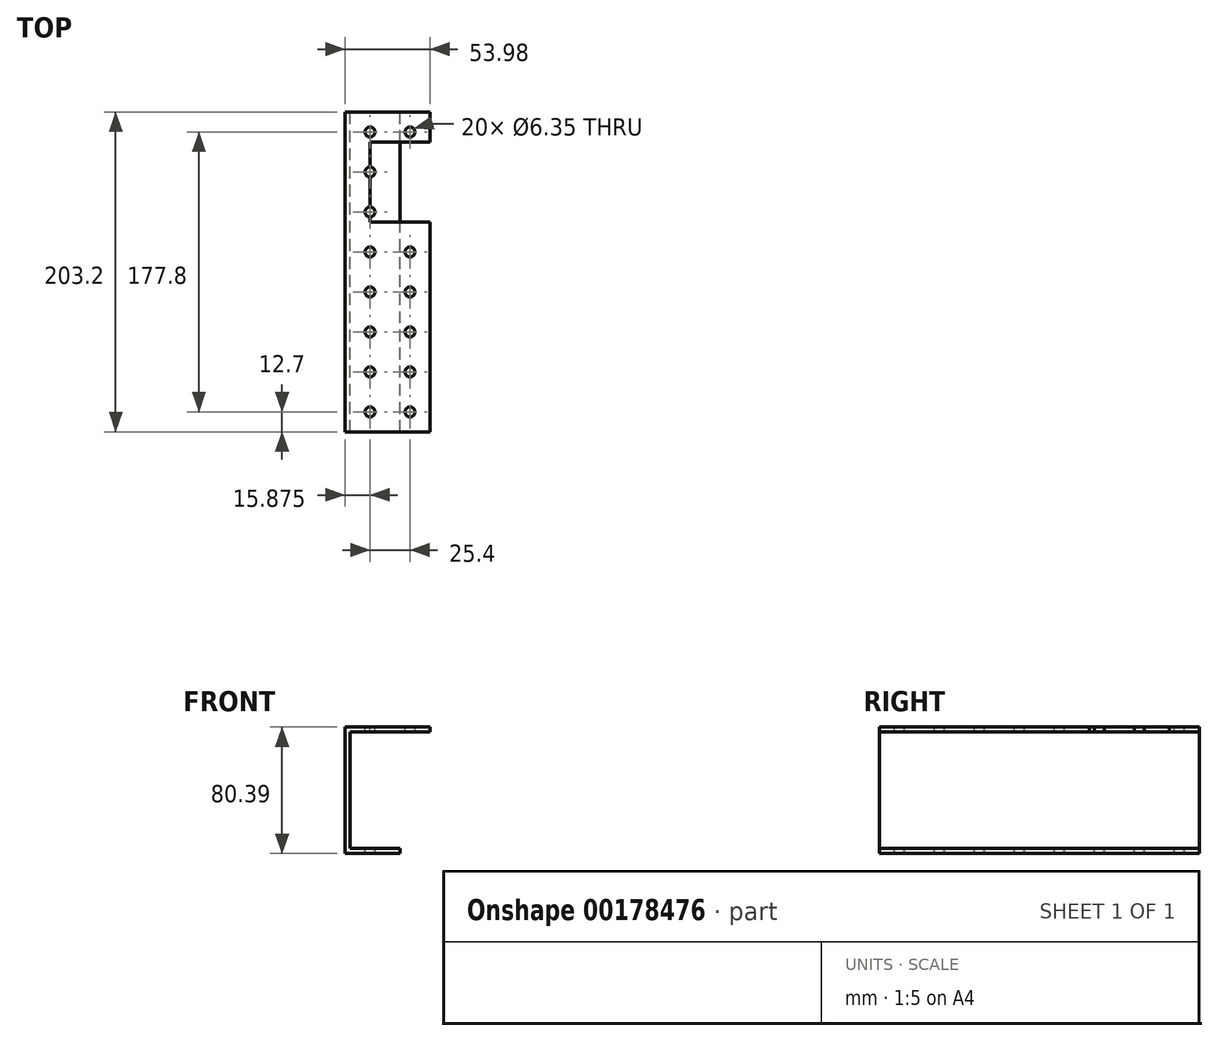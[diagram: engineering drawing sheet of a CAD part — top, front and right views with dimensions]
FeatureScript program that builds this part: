
annotation { "Feature Type Name" : "Feature", "Feature Type Description" : "" }
export const myFeature = defineFeature(function(context is Context, id is Id, definition is map)
    precondition{}
    {
        {
            var Q0;
            Q0=qCreatedBy(makeId("Front.planeOp"),FACE);
            var sketch = newSketch(context, id + "F0", { "sketchPlane" : qUnion([Q0])});
            skLineSegment(sketch, "E0", {"start": v(0, 44.52) * mm, "end": v(0, -35.87) * mm});
            skLineSegment(sketch, "E1", {"start": v(0, 44.52) * mm, "end": v(53.98, 44.52) * mm});
            skLineSegment(sketch, "E2", {"start": v(0, -35.87) * mm, "end": v(34.93, -35.87) * mm});
            skLineSegment(sketch, "E3", {"start": v(34.93, -35.87) * mm, "end": v(34.93, -32.7) * mm});
            skLineSegment(sketch, "E4", {"start": v(34.93, -32.7) * mm, "end": v(3.18, -32.7) * mm});
            skLineSegment(sketch, "E5", {"start": v(3.18, -32.7) * mm, "end": v(3.18, 41.34) * mm});
            skLineSegment(sketch, "E6", {"start": v(3.18, 41.34) * mm, "end": v(53.98, 41.34) * mm});
            skLineSegment(sketch, "E7", {"start": v(53.98, 41.34) * mm, "end": v(53.98, 44.52) * mm});
            skSolve(sketch);
        }
        {
            var Q0;
            Q0=makeQuery(id+"F0.imprint","IMPRINT",FACE,{"disambiguationData":[TD([[makeQuery(id+"F0.imprint","IMPRINT",EDGE,{"derivedFrom":sQuery(id+"F0.wireOp",EDGE,"E0")}),1.0]])]});
            extrude(context, id + "F1", {"entities" : qUnion([Q0]), "depth" : 203.2 * mm});
        }
        {
            var Q0;
            Q0=makeQuery(id+"F1.opExtrude","SWEPT_FACE",FACE,{"disambiguationData":[OSD([sQuery(id+"F0.wireOp",EDGE,"E1")])]});
            var sketch = newSketch(context, id + "F2", { "sketchPlane" : qUnion([Q0])});
            skLineSegment(sketch, "E8.bottom", {"start": v(53.98, -19.05) * mm, "end": v(15.87, -19.05) * mm});
            skLineSegment(sketch, "E8.top", {"start": v(53.98, -69.85) * mm, "end": v(15.88, -69.85) * mm});
            skLineSegment(sketch, "E8.left", {"start": v(53.98, -19.05) * mm, "end": v(53.98, -69.85) * mm});
            skLineSegment(sketch, "E8.right", {"start": v(15.87, -19.05) * mm, "end": v(15.88, -69.85) * mm});
            skLineSegment(sketch, "E9", {"start": v(15.24, -37.47) * mm, "end": v(15.24, -18.42) * mm});
            skLineSegment(sketch, "E10", {"start": v(15.24, -18.42) * mm, "end": v(-22.86, -18.42) * mm});
            skLineSegment(sketch, "E11", {"start": v(-22.86, -18.42) * mm, "end": v(-22.86, 32.38) * mm});
            skLineSegment(sketch, "E12", {"start": v(-22.86, 32.38) * mm, "end": v(15.24, 32.38) * mm});
            skLineSegment(sketch, "E13", {"start": v(15.24, 32.38) * mm, "end": v(15.24, -18.42) * mm});
            skSolve(sketch);
        }
        {
            var Q0;
            {var subQ10=sQuery(id+"F2.wireOp",EDGE,"E8.left");Q0=makeQuery(id+"F2.imprint","IMPRINT",FACE,{"disambiguationData":[TD([[makeQuery(id+"F2.imprint","IMPRINT",EDGE,{"derivedFrom":subQ10}),1.0]])]});}
            extrude(context, id + "F3", {"entities" : qUnion([Q0]), "operationType" : NewBodyOperationType.REMOVE, "oppositeDirection" : true, "depth" : 25.4 * mm});
        }
        {
            var Q0;
            Q0=makeQuery(id+"F1.opExtrude","SWEPT_FACE",FACE,{"disambiguationData":[OSD([sQuery(id+"F0.wireOp",EDGE,"E1")])]});
            var sketch = newSketch(context, id + "F4", { "sketchPlane" : qUnion([Q0])});
            skCircle(sketch, "E14", {"center": v(41.27, -190.5) * mm, "radius": 3.18 * mm});
            skCircle(sketch, "E15.0.1.0", {"center": v(41.27, -165.1) * mm, "radius": 3.18 * mm});
            skCircle(sketch, "E15.0.2.0", {"center": v(41.27, -139.7) * mm, "radius": 3.18 * mm});
            skCircle(sketch, "E15.0.3.0", {"center": v(41.27, -114.3) * mm, "radius": 3.18 * mm});
            skCircle(sketch, "E15.0.4.0", {"center": v(41.27, -88.9) * mm, "radius": 3.18 * mm});
            skCircle(sketch, "E15.0.5.0", {"center": v(41.27, -63.5) * mm, "radius": 3.18 * mm});
            skCircle(sketch, "E15.0.6.0", {"center": v(41.27, -38.1) * mm, "radius": 3.18 * mm});
            skCircle(sketch, "E15.0.7.0", {"center": v(41.27, -12.7) * mm, "radius": 3.18 * mm});
            skCircle(sketch, "E15.1.0.0", {"center": v(15.87, -190.5) * mm, "radius": 3.18 * mm});
            skCircle(sketch, "E15.1.1.0", {"center": v(15.87, -165.1) * mm, "radius": 3.18 * mm});
            skCircle(sketch, "E15.1.2.0", {"center": v(15.87, -139.7) * mm, "radius": 3.18 * mm});
            skCircle(sketch, "E15.1.3.0", {"center": v(15.87, -114.3) * mm, "radius": 3.18 * mm});
            skCircle(sketch, "E15.1.4.0", {"center": v(15.87, -88.9) * mm, "radius": 3.18 * mm});
            skCircle(sketch, "E15.1.5.0", {"center": v(15.87, -63.5) * mm, "radius": 3.18 * mm});
            skCircle(sketch, "E15.1.6.0", {"center": v(15.87, -38.1) * mm, "radius": 3.18 * mm});
            skCircle(sketch, "E15.1.7.0", {"center": v(15.87, -12.7) * mm, "radius": 3.18 * mm});
            skLineSegment(sketch, "E15.direction1", {"start": v(41.27, -190.5) * mm, "end": v(15.87, -190.5) * mm, "construction": true});
            skLineSegment(sketch, "E15.direction2", {"start": v(41.27, -190.5) * mm, "end": v(41.27, -165.1) * mm, "construction": true});
            skSolve(sketch);
        }
        {
            var Q0;
            Q0 = qSketchRegion(id + "F4", true);
            extrude(context, id + "F5", {"entities" : qUnion([Q0]), "operationType" : NewBodyOperationType.REMOVE, "oppositeDirection" : true, "depth" : 101.6 * mm});
        }
    });
